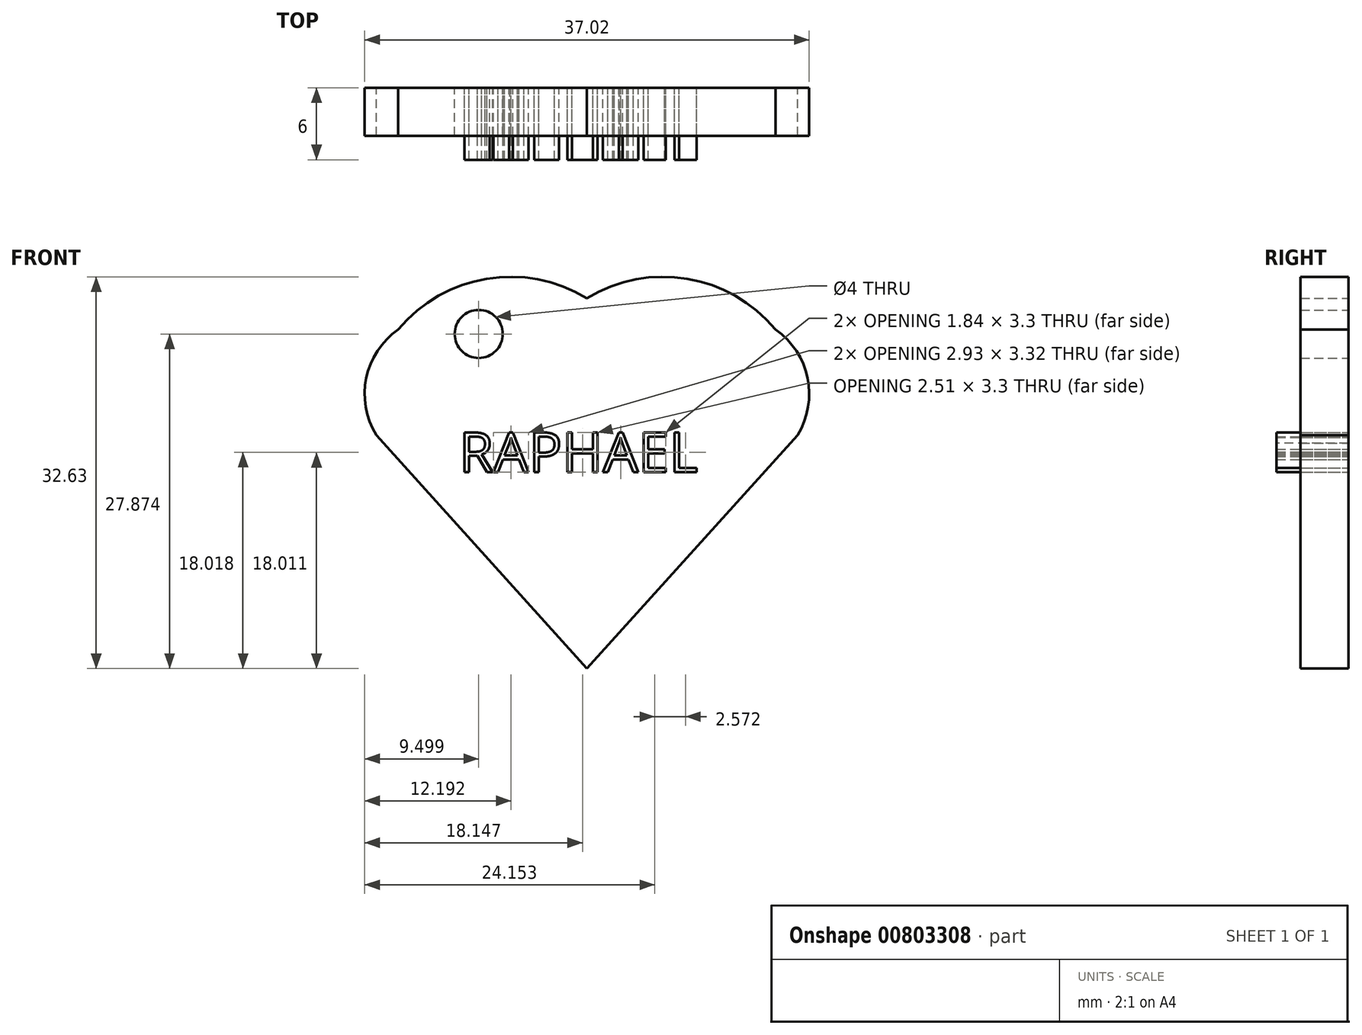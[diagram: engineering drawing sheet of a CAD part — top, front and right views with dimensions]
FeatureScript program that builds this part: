
annotation { "Feature Type Name" : "Feature", "Feature Type Description" : "" }
export const myFeature = defineFeature(function(context is Context, id is Id, definition is map)
    precondition{}
    {
        {
            var Q0;
            Q0=qCreatedBy(makeId("Front.planeOp"),FACE);
            var sketch = newSketch(context, id + "F0", { "sketchPlane" : qUnion([Q0])});
            skArc(sketch, "E0", {"start": v(0, 18.46) * mm, "mid": v(-8.34, 20.08) * mm, "end": v(-15.7, 15.85) * mm});
            skArc(sketch, "E1", {"start": v(-15.7, 15.85) * mm, "mid": v(-18.37, 11.82) * mm, "end": v(-17.55, 7.07) * mm});
            skLineSegment(sketch, "E2", {"start": v(-17.55, 7.07) * mm, "end": v(0, -12.4) * mm});
            skArc(sketch, "E3.MirrorCS", {"start": v(0, 18.46) * mm, "mid": v(8.34, 20.08) * mm, "end": v(15.7, 15.85) * mm});
            skArc(sketch, "E4.MirrorCS", {"start": v(15.7, 15.85) * mm, "mid": v(18.37, 11.82) * mm, "end": v(17.55, 7.07) * mm});
            skLineSegment(sketch, "E5.MirrorCS", {"start": v(17.55, 7.07) * mm, "end": v(0, -12.4) * mm});
            skText(sketch, "E6", { "text": "RAPHAEL\n", "fontName": "OpenSans-Regular.ttf"});
            skCircle(sketch, "E7", {"center": v(-9.01, 15.48) * mm, "radius": 2 * mm});
            const initialGuessF0  = {"E6": [-0.01064, 0.00397, 1, 0, 0.00333]};
            skSetInitialGuess(sketch, initialGuessF0);
            skSolve(sketch);
        }
        {
            var Q0;
            Q0=makeQuery(id+"F0.imprint","IMPRINT",FACE,{"disambiguationData":[TD([[makeQuery(id+"F0.imprint","IMPRINT",EDGE,{"derivedFrom":sQuery(id+"F0.wireOp",EDGE,"E0")}),1.0]])]});
            var Q1;
            Q1=makeQuery(id+"F0.imprint","IMPRINT",FACE,{"disambiguationData":[TD([[makeQuery(id+"F0.imprint","IMPRINT",EDGE,{"derivedFrom":sQuery(id+"F0.wireOp",EDGE,"E6.sketch_text.stroke-26")}),1.0]])]});
            var Q2;
            Q2=makeQuery(id+"F0.imprint","IMPRINT",FACE,{"disambiguationData":[TD([[makeQuery(id+"F0.imprint","IMPRINT",EDGE,{"derivedFrom":sQuery(id+"F0.wireOp",EDGE,"E6.sketch_text.stroke-11")}),1.0]])]});
            var Q3;
            Q3=makeQuery(id+"F0.imprint","IMPRINT",FACE,{"disambiguationData":[TD([[makeQuery(id+"F0.imprint","IMPRINT",EDGE,{"derivedFrom":sQuery(id+"F0.wireOp",EDGE,"E6.sketch_text.stroke-39")}),1.0]])]});
            var Q4;
            Q4=makeQuery(id+"F0.imprint","IMPRINT",FACE,{"disambiguationData":[TD([[makeQuery(id+"F0.imprint","IMPRINT",EDGE,{"derivedFrom":sQuery(id+"F0.wireOp",EDGE,"E6.sketch_text.stroke-66")}),1.0]])]});
            extrude(context, id + "F1", {"entities" : qUnion([Q0, Q1, Q2, Q3, Q4]), "depth" : 4 * mm, "offsetDistance" : 25 * mm});
        }
        {
            var Q0;
            Q0=makeQuery(id+"F0.imprint","IMPRINT",FACE,{"disambiguationData":[TD([[makeQuery(id+"F0.imprint","IMPRINT",EDGE,{"derivedFrom":sQuery(id+"F0.wireOp",EDGE,"E6.sketch_text.stroke-0")}),-1.0]])]});
            var Q1;
            Q1=makeQuery(id+"F0.imprint","IMPRINT",FACE,{"disambiguationData":[TD([[makeQuery(id+"F0.imprint","IMPRINT",EDGE,{"derivedFrom":sQuery(id+"F0.wireOp",EDGE,"E6.sketch_text.stroke-18")}),-1.0]])]});
            var Q2;
            Q2=makeQuery(id+"F0.imprint","IMPRINT",FACE,{"disambiguationData":[TD([[makeQuery(id+"F0.imprint","IMPRINT",EDGE,{"derivedFrom":sQuery(id+"F0.wireOp",EDGE,"E6.sketch_text.stroke-31")}),-1.0]])]});
            var Q3;
            Q3=makeQuery(id+"F0.imprint","IMPRINT",FACE,{"disambiguationData":[TD([[makeQuery(id+"F0.imprint","IMPRINT",EDGE,{"derivedFrom":sQuery(id+"F0.wireOp",EDGE,"E6.sketch_text.stroke-46")}),-1.0]])]});
            var Q4;
            Q4=makeQuery(id+"F0.imprint","IMPRINT",FACE,{"disambiguationData":[TD([[makeQuery(id+"F0.imprint","IMPRINT",EDGE,{"derivedFrom":sQuery(id+"F0.wireOp",EDGE,"E6.sketch_text.stroke-58")}),-1.0]])]});
            var Q5;
            Q5=makeQuery(id+"F0.imprint","IMPRINT",FACE,{"disambiguationData":[TD([[makeQuery(id+"F0.imprint","IMPRINT",EDGE,{"derivedFrom":sQuery(id+"F0.wireOp",EDGE,"E6.sketch_text.stroke-71")}),-1.0]])]});
            var Q6;
            Q6=makeQuery(id+"F0.imprint","IMPRINT",FACE,{"disambiguationData":[TD([[makeQuery(id+"F0.imprint","IMPRINT",EDGE,{"derivedFrom":sQuery(id+"F0.wireOp",EDGE,"E6.sketch_text.stroke-83")}),-1.0]])]});
            extrude(context, id + "F2", {"entities" : qUnion([Q0, Q1, Q2, Q3, Q4, Q5, Q6]), "depth" : 6 * mm, "offsetDistance" : 25 * mm});
        }
    });
